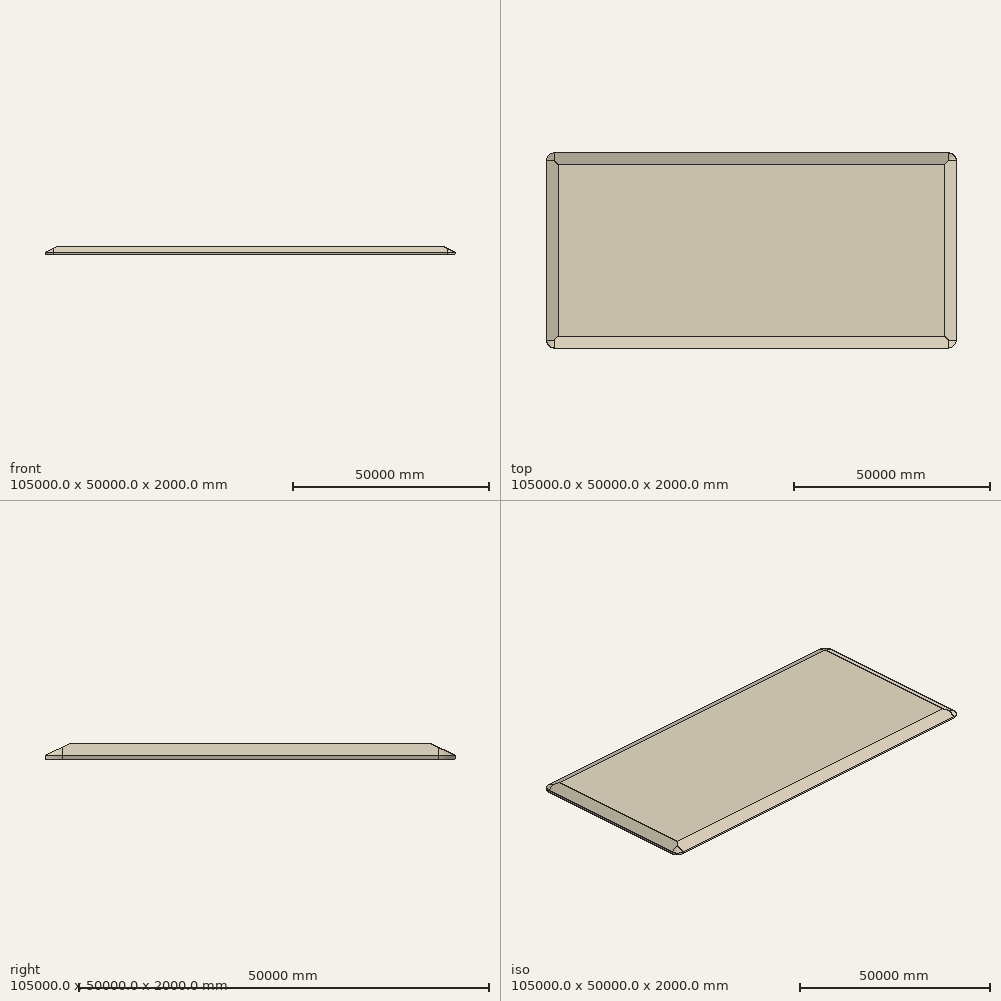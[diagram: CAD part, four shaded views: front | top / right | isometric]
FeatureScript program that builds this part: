
annotation { "Feature Type Name" : "Feature", "Feature Type Description" : "" }
export const myFeature = defineFeature(function(context is Context, id is Id, definition is map)
    precondition{}
    {
        {
            var Q0;
            Q0=qCreatedBy(makeId("Top.planeOp"),FACE);
            var sketch = newSketch(context, id + "F0", { "sketchPlane" : qUnion([Q0])});
            skLineSegment(sketch, "E0.bottom", {"start": v(-102898.3, 52005.58) * mm, "end": v(-1998.3, 52005.58) * mm});
            skLineSegment(sketch, "E0.top", {"start": v(-102898.3, 2005.58) * mm, "end": v(-1998.3, 2005.58) * mm});
            skLineSegment(sketch, "E0.left", {"start": v(-104948.3, 49955.58) * mm, "end": v(-104948.3, 4055.58) * mm});
            skLineSegment(sketch, "E0.right", {"start": v(51.7, 49955.58) * mm, "end": v(51.7, 4055.58) * mm});
            skPoint(sketch, "E1.visualSharp", {"position": v(-104948.3, 52005.58) * mm});
            skArc(sketch, "E1.filletArc", {"start": v(-102898.3, 52005.58) * mm, "mid": v(-104347.86, 51405.15) * mm, "end": v(-104948.3, 49955.58) * mm});
            skPoint(sketch, "E2.visualSharp", {"position": v(-104948.3, 2005.58) * mm});
            skArc(sketch, "E2.filletArc", {"start": v(-104948.3, 4055.58) * mm, "mid": v(-104347.86, 2606.01) * mm, "end": v(-102898.3, 2005.58) * mm});
            skPoint(sketch, "E3.visualSharp", {"position": v(51.7, 2005.58) * mm});
            skArc(sketch, "E3.filletArc", {"start": v(-1998.3, 2005.58) * mm, "mid": v(-548.72, 2606.01) * mm, "end": v(51.7, 4055.58) * mm});
            skPoint(sketch, "E4.visualSharp", {"position": v(51.7, 52005.58) * mm});
            skArc(sketch, "E4.filletArc", {"start": v(51.7, 49955.58) * mm, "mid": v(-548.72, 51405.15) * mm, "end": v(-1998.3, 52005.58) * mm});
            skSolve(sketch);
        }
        {
            var Q0;
            Q0=makeQuery(id+"F0.imprint","IMPRINT",FACE,{"disambiguationData":[TD([[makeQuery(id+"F0.imprint","IMPRINT",EDGE,{"derivedFrom":sQuery(id+"F0.wireOp",EDGE,"E0.bottom")}),-1.0]])]});
            extrude(context, id + "F1", {"entities" : qUnion([Q0]), "depth" : 1500 * mm, "hasDraft" : true, "draftAngle" : 64 * degree, "draftPullDirection" : true});
        }
        {
            var Q0;
            Q0=makeQuery(id+"F1.opExtrude","CAP_FACE",FACE,{"disambiguationData":[OSD([sQuery(id+"F0.wireOp",EDGE,"E0.bottom"),sQuery(id+"F0.wireOp",EDGE,"E0.top"),sQuery(id+"F0.wireOp",EDGE,"E0.left"),sQuery(id+"F0.wireOp",EDGE,"E0.right"),sQuery(id+"F0.wireOp",EDGE,"E1.filletArc"),sQuery(id+"F0.wireOp",EDGE,"E2.filletArc"),sQuery(id+"F0.wireOp",EDGE,"E3.filletArc"),sQuery(id+"F0.wireOp",EDGE,"E4.filletArc")])],"isStart":true});
            extrude(context, id + "F2", {"entities" : qUnion([Q0]), "operationType" : NewBodyOperationType.ADD, "depth" : 500 * mm});
        }
    });
